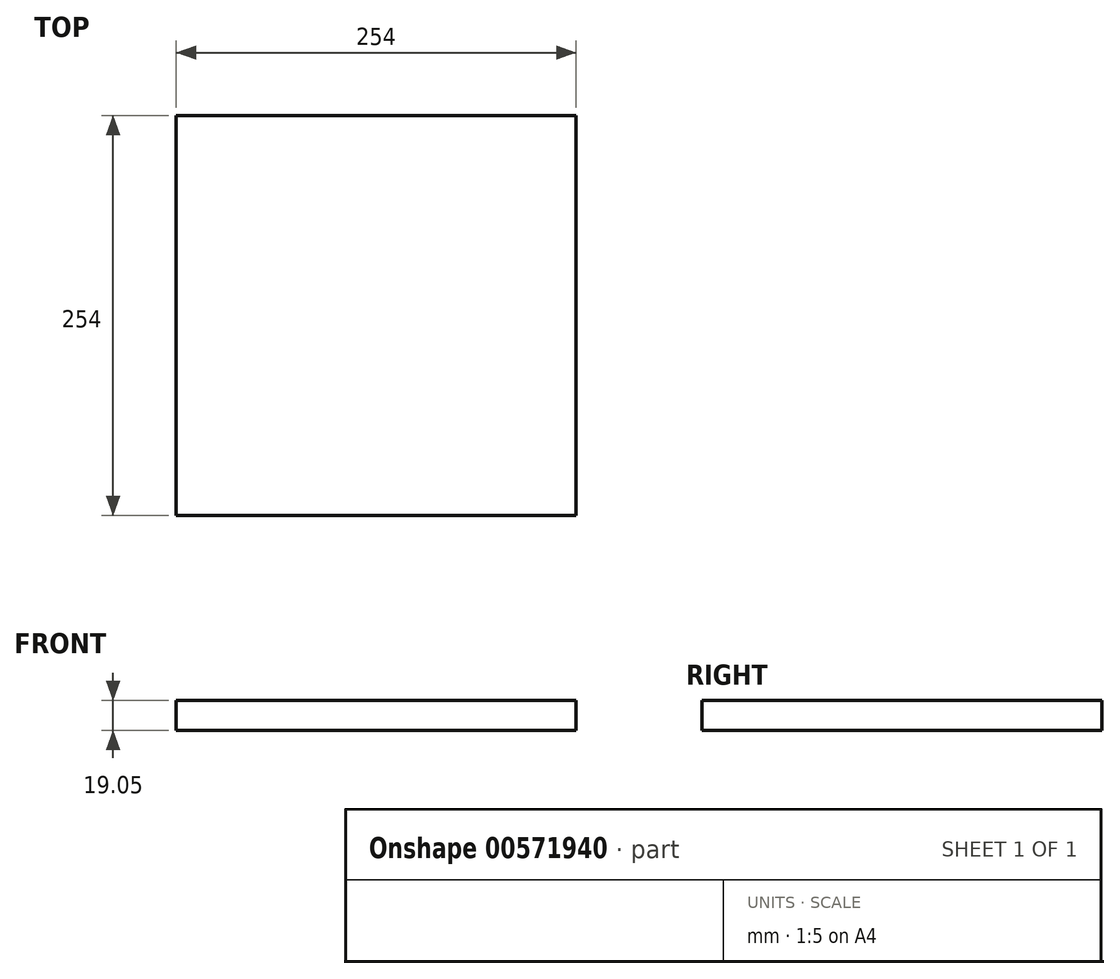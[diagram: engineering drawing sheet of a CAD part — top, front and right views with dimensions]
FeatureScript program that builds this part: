
annotation { "Feature Type Name" : "Feature", "Feature Type Description" : "" }
export const myFeature = defineFeature(function(context is Context, id is Id, definition is map)
    precondition{}
    {
        {
            var Q0;
            Q0=qCreatedBy(makeId("Top.planeOp"),FACE);
            var sketch = newSketch(context, id + "F0", { "sketchPlane" : qUnion([Q0])});
            skLineSegment(sketch, "E0.bottom", {"start": v(127, -127) * mm, "end": v(-127, -127) * mm});
            skLineSegment(sketch, "E0.top", {"start": v(127, 127) * mm, "end": v(-127, 127) * mm});
            skLineSegment(sketch, "E0.left", {"start": v(127, -127) * mm, "end": v(127, 127) * mm});
            skLineSegment(sketch, "E0.right", {"start": v(-127, -127) * mm, "end": v(-127, 127) * mm});
            skPoint(sketch, "E0.middle", {"position": v(0, 0) * mm});
            skSolve(sketch);
        }
        {
            var Q0;
            Q0 = qSketchRegion(id + "F0", true);
            extrude(context, id + "F1", {"entities" : qUnion([Q0]), "depth" : 19.05 * mm, "offsetDistance" : 25.4 * mm});
        }
    });
